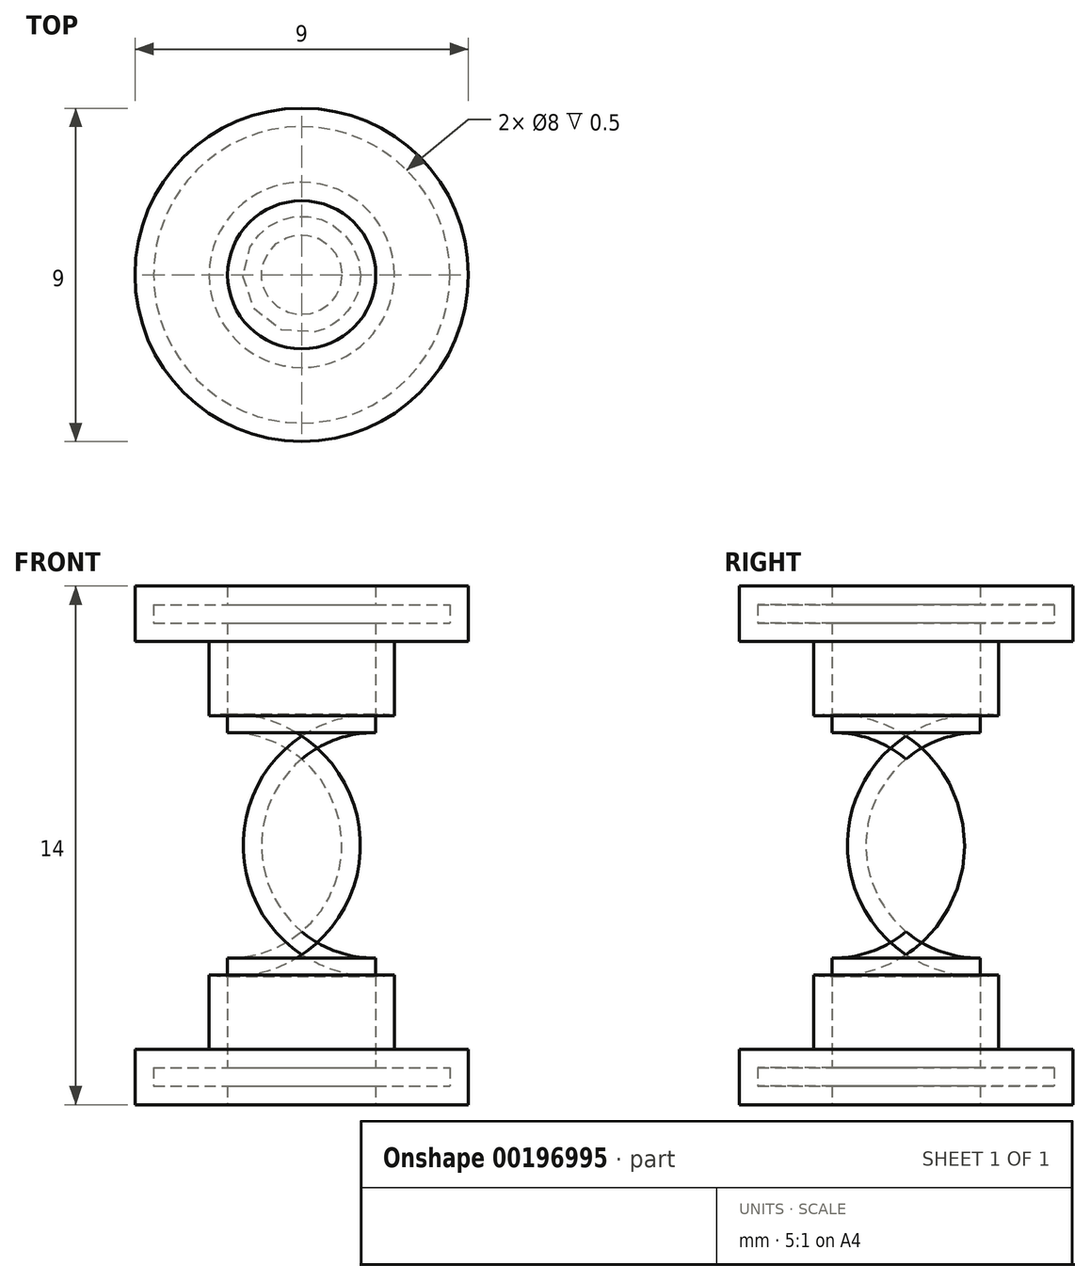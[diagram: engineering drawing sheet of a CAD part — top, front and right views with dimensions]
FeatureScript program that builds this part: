
annotation { "Feature Type Name" : "Feature", "Feature Type Description" : "" }
export const myFeature = defineFeature(function(context is Context, id is Id, definition is map)
    precondition{}
    {
        {
            var Q0;
            Q0=qCreatedBy(makeId("Front.planeOp"),FACE);
            var sketch = newSketch(context, id + "F0", { "sketchPlane" : qUnion([Q0])});
            skLineSegment(sketch, "E0", {"start": v(0, 0) * mm, "end": v(0, 14) * mm, "construction": true});
            skLineSegment(sketch, "E1", {"start": v(0, 7) * mm, "end": v(5.5, 7) * mm, "construction": true});
            skLineSegment(sketch, "E2", {"start": v(0, 1.5) * mm, "end": v(2.5, 1.5) * mm, "construction": true});
            skLineSegment(sketch, "E3", {"start": v(2, 0) * mm, "end": v(4.5, 0) * mm});
            skLineSegment(sketch, "E4", {"start": v(4.5, 0) * mm, "end": v(4.5, 1.5) * mm});
            skLineSegment(sketch, "E5", {"start": v(4.5, 1.5) * mm, "end": v(2.5, 1.5) * mm});
            skLineSegment(sketch, "E6", {"start": v(2.5, 1.5) * mm, "end": v(2.5, 3.5) * mm});
            skLineSegment(sketch, "E7", {"start": v(2, 14) * mm, "end": v(4.5, 14) * mm});
            skLineSegment(sketch, "E8", {"start": v(4.5, 14) * mm, "end": v(4.5, 12.5) * mm});
            skLineSegment(sketch, "E9", {"start": v(4.5, 12.5) * mm, "end": v(2.5, 12.5) * mm});
            skLineSegment(sketch, "E10", {"start": v(2.5, 12.5) * mm, "end": v(2.5, 10.5) * mm});
            skArc(sketch, "E11", {"start": v(2.5, 3.5) * mm, "mid": v(5.5, 7) * mm, "end": v(2.5, 10.5) * mm});
            skLineSegment(sketch, "E12.0", {"start": v(2, 0.5) * mm, "end": v(4, 0.5) * mm});
            skLineSegment(sketch, "E12.1", {"start": v(4, 0.5) * mm, "end": v(4, 1) * mm});
            skLineSegment(sketch, "E12.2", {"start": v(4, 1) * mm, "end": v(2, 1) * mm});
            skLineSegment(sketch, "E12.3", {"start": v(2, 1) * mm, "end": v(2, 3.96) * mm});
            skArc(sketch, "E12.4", {"start": v(2, 3.96) * mm, "mid": v(5, 7) * mm, "end": v(2, 10.04) * mm});
            skLineSegment(sketch, "E12.5", {"start": v(2, 13.5) * mm, "end": v(4, 13.5) * mm});
            skLineSegment(sketch, "E12.6", {"start": v(4, 13.5) * mm, "end": v(4, 13) * mm});
            skLineSegment(sketch, "E12.7", {"start": v(4, 13) * mm, "end": v(2, 13) * mm});
            skLineSegment(sketch, "E12.8", {"start": v(2, 13) * mm, "end": v(2, 10.04) * mm});
            skLineSegment(sketch, "E13", {"start": v(2, 13.5) * mm, "end": v(2, 14) * mm});
            skPoint(sketch, "E14.orphan", {"position": v(0, 13.5) * mm});
            skLineSegment(sketch, "E15", {"start": v(2, 0.5) * mm, "end": v(2, 0) * mm});
            skPoint(sketch, "E16.orphan", {"position": v(0, 0.5) * mm});
            skSolve(sketch);
        }
        {
            var Q0;
            Q0 = qSketchRegion(id + "F0", true);
            var Q1;
            Q1=sQuery(id+"F0.wireOp",EDGE,"E0");
            revolve(context, id + "F1", {"entities" : qUnion([Q0]), "axis" : qUnion([Q1]), "revolveType" : RevolveType.FULL});
        }
    });
